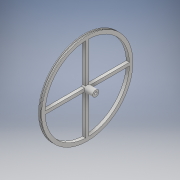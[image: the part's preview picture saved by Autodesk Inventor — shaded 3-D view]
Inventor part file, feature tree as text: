
AUTODESK INVENTOR PART (.ipt)
format: ipt  version: 2018 (Build 220112000, 112)  size: 335,360 bytes
history: native  units: mm
features: extrude x8, sketch x8, pattern_circular x1
ambient origin geometry x8: Origin, YZ Plane, XZ Plane, XY Plane, X Axis, Y Axis, Z Axis, Center Point
bodies: Solid1 (feature_tree)
feature tree (17):
  extrude  "Extrusion1"  Depth=2.0mm TaperAngle=0.0deg
  extrude  "Extrusion2"  Depth=1.0mm TaperAngle=0.0deg
  extrude  "Extrusion3"  Depth=1.0mm
  extrude  "Extrusion4"  Depth=3.0mm
  extrude  "Extrusion5"  Depth=5.0mm TaperAngle=0.0deg
  extrude  "Extrusion6"  Depth=4.0mm
  pattern_circular  "Circular Pattern1"  Count=4 Angle=360.0deg
  extrude  "Extrusion7"  Depth=15.0mm TaperAngle=0.0deg
  extrude  "Extrusion8"  Depth=15.0mm
  sketch  "Sketch1"  dims[d0=115.0mm d1=2.0mm d2=0.0mm]
  sketch  "Sketch2"  dims[d3=117.0mm d4=1.0mm d5=0.0mm]
  sketch  "Sketch3"  dims[d6=1.0mm d7=0.0mm d8=108.0mm]
  sketch  "Sketch4"  dims[d9=5.0mm d10=0.0mm d11=3.0mm]
  sketch  "Sketch5"  dims[d12=7.0mm d13=5.0mm d14=0.0mm]
  sketch  "Sketch6"  dims[d15=2.0mm d16=4.0mm]
  sketch  "Sketch7"  dims[d17=4.0mm d18=0.0mm d19=40.0mm d20=360.0deg]
  sketch  "Sketch8"  dims[d22=8.0mm d23=15.0mm d24=0.0mm d25=3.25mm d26=100.0mm d27=0.0mm]
